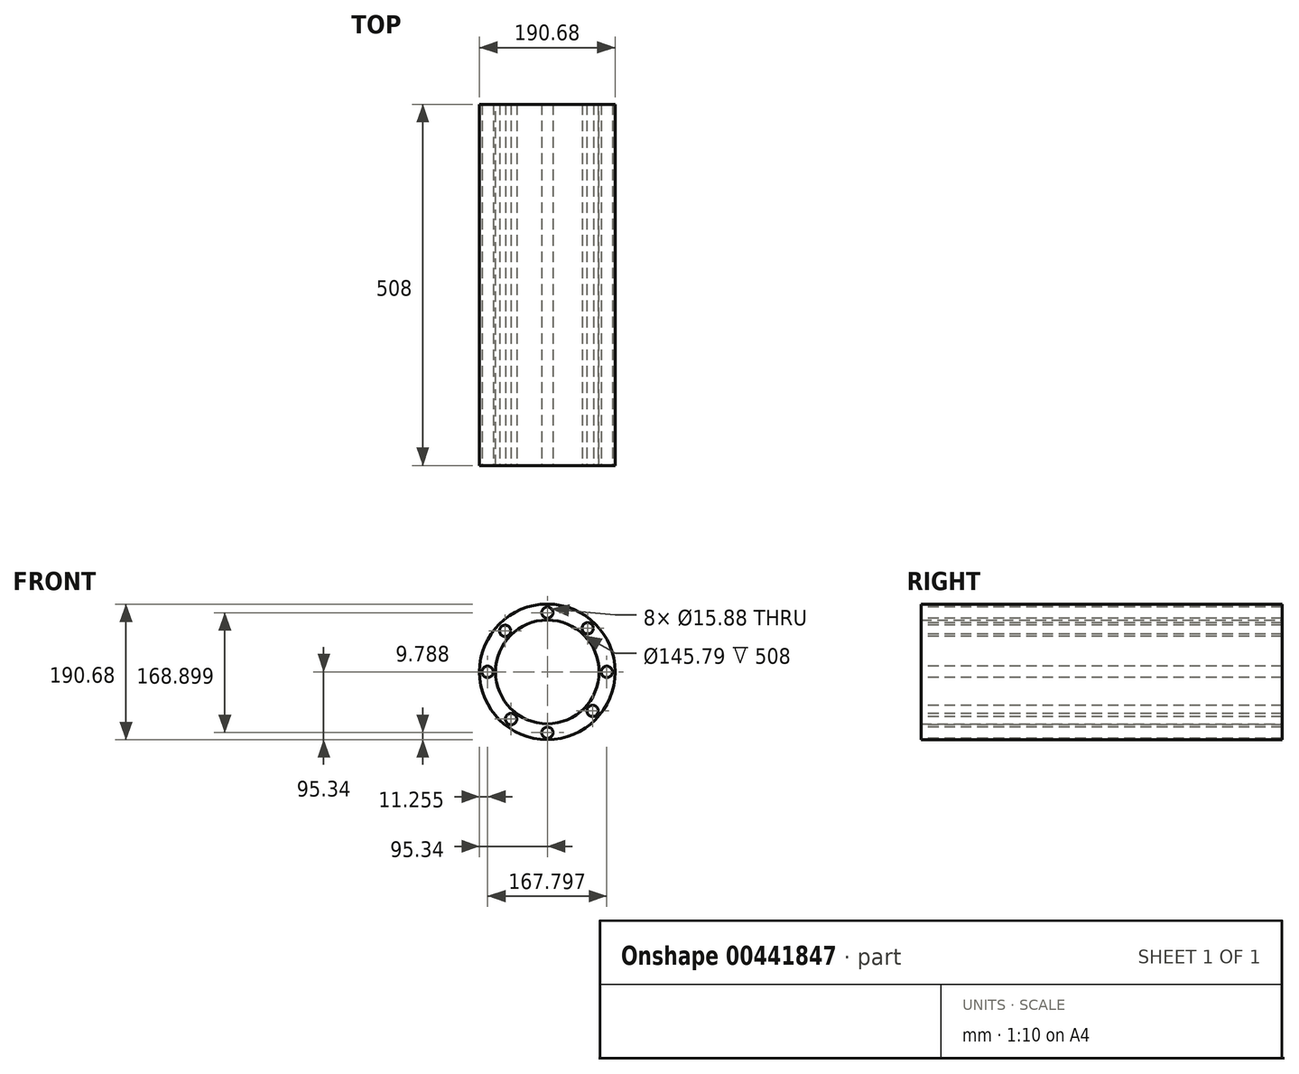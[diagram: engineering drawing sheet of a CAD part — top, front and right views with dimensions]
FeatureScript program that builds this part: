
annotation { "Feature Type Name" : "Feature", "Feature Type Description" : "" }
export const myFeature = defineFeature(function(context is Context, id is Id, definition is map)
    precondition{}
    {
        {
            var Q0;
            Q0=qCreatedBy(makeId("Front.planeOp"),FACE);
            var sketch = newSketch(context, id + "F0", { "sketchPlane" : qUnion([Q0])});
            skCircle(sketch, "E0", {"center": v(0, 0) * mm, "radius": 95.34 * mm});
            skCircle(sketch, "E1", {"center": v(0, 0) * mm, "radius": 72.9 * mm});
            skSolve(sketch);
        }
        {
            var Q0;
            Q0=makeQuery(id+"F0.imprint","IMPRINT",FACE,{"disambiguationData":[TD([[makeQuery(id+"F0.imprint","IMPRINT",EDGE,{"derivedFrom":sQuery(id+"F0.wireOp",EDGE,"E0")}),1.0]])]});
            extrude(context, id + "F1", {"entities" : qUnion([Q0]), "depth" : 254 * mm});
        }
        {
            var Q0;
            Q0=makeQuery(id+"F1.opExtrude","CAP_FACE",FACE,{"disambiguationData":[OSD([sQuery(id+"F0.wireOp",EDGE,"E0"),sQuery(id+"F0.wireOp",EDGE,"E1")])],"isStart":false});
            extrude(context, id + "F2", {"entities" : qUnion([Q0]), "operationType" : NewBodyOperationType.ADD, "depth" : 254 * mm});
        }
        {
            var Q0;
            Q0=makeQuery(id+"F2.opExtrude","CAP_FACE",FACE,{"disambiguationData":[OSD([sQuery(id+"F0.wireOp",EDGE,"E0"),sQuery(id+"F0.wireOp",EDGE,"E1")])],"isStart":false});
            var sketch = newSketch(context, id + "F3", { "sketchPlane" : qUnion([Q0])});
            skCircle(sketch, "E2", {"center": v(-84.08, 0) * mm, "radius": 8.03 * mm});
            skCircle(sketch, "E3", {"center": v(83.71, 0) * mm, "radius": 7.36 * mm});
            skCircle(sketch, "E4", {"center": v(0, 83.35) * mm, "radius": 7.07 * mm});
            skCircle(sketch, "E5", {"center": v(-59.39, 57.77) * mm, "radius": 7.23 * mm});
            skCircle(sketch, "E6", {"center": v(56.81, 61.3) * mm, "radius": 6.92 * mm});
            skCircle(sketch, "E7", {"center": v(-51.01, -66.37) * mm, "radius": 7.33 * mm});
            skCircle(sketch, "E8", {"center": v(63.65, -54.9) * mm, "radius": 7.41 * mm});
            skCircle(sketch, "E9", {"center": v(0, -85.55) * mm, "radius": 7.27 * mm});
            skSolve(sketch);
        }
        {
            var Q0;
            Q0=sQuery(id+"F3.wireOp",VERTEX,"E5.center");
            var Q1;
            Q1=sQuery(id+"F3.wireOp",VERTEX,"E2.center");
            var Q2;
            Q2=sQuery(id+"F3.wireOp",VERTEX,"E4.center");
            var Q3;
            Q3=sQuery(id+"F3.wireOp",VERTEX,"E6.center");
            var Q4;
            Q4=sQuery(id+"F3.wireOp",VERTEX,"E3.center");
            var Q5;
            Q5=sQuery(id+"F3.wireOp",VERTEX,"E8.center");
            var Q6;
            Q6=sQuery(id+"F3.wireOp",VERTEX,"E9.center");
            var Q7;
            Q7=sQuery(id+"F3.wireOp",VERTEX,"E7.center");
            var Q8;
            Q8=makeQuery(id+"F1.opExtrude","SWEPT_BODY",BODY,{"disambiguationData":[OSD([sQuery(id+"F0.wireOp",EDGE,"E0"),sQuery(id+"F0.wireOp",EDGE,"E1")])]});
            hole(context, id + "F4", {"style" : HoleStyle.SIMPLE, "endStyle" : HoleEndStyle.THROUGH, "holeDiameter" : 15.88 * mm, "isTappedThrough" : true, "tappedDepth" : 12.7 * mm, "tapClearance" : 3, "locations" : qUnion([Q0, Q1, Q2, Q3, Q4, Q5, Q6, Q7]), "scope" : qUnion([Q8])});
        }
    });
